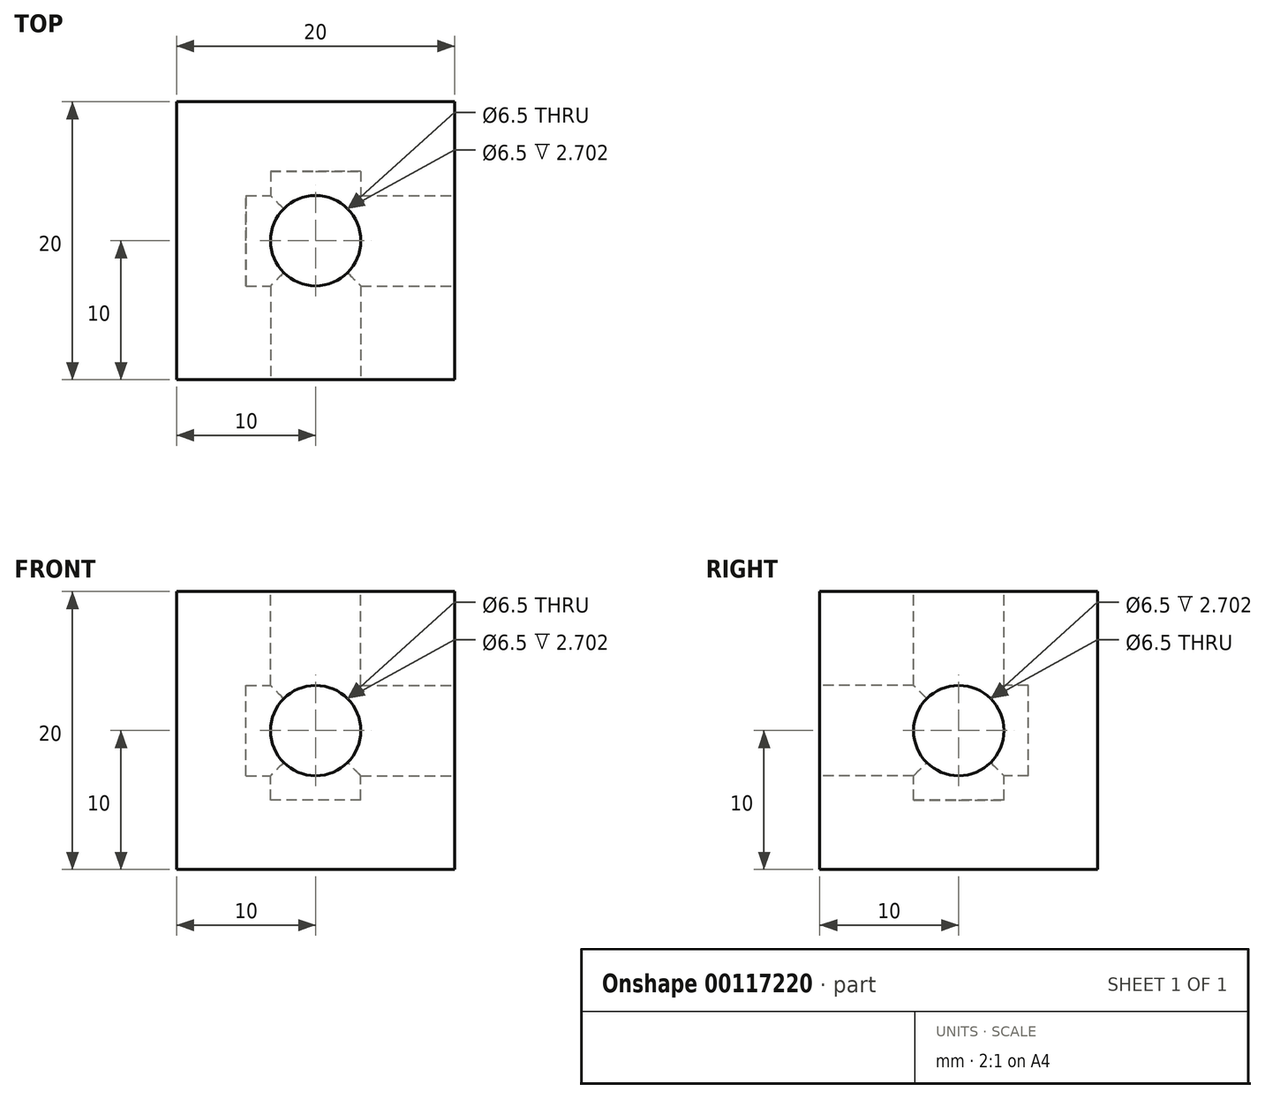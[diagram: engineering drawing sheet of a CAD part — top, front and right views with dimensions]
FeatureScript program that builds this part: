
annotation { "Feature Type Name" : "Feature", "Feature Type Description" : "" }
export const myFeature = defineFeature(function(context is Context, id is Id, definition is map)
    precondition{}
    {
        {
            var Q0;
            Q0=qCreatedBy(makeId("Top.planeOp"),FACE);
            var sketch = newSketch(context, id + "F0", { "sketchPlane" : qUnion([Q0])});
            skLineSegment(sketch, "E0.bottom", {"start": v(10, -10) * mm, "end": v(-10, -10) * mm});
            skLineSegment(sketch, "E0.top", {"start": v(10, 10) * mm, "end": v(-10, 10) * mm});
            skLineSegment(sketch, "E0.left", {"start": v(10, -10) * mm, "end": v(10, 10) * mm});
            skLineSegment(sketch, "E0.right", {"start": v(-10, -10) * mm, "end": v(-10, 10) * mm});
            skPoint(sketch, "E0.middle", {"position": v(0, 0) * mm});
            skSolve(sketch);
        }
        {
            var Q0;
            Q0=makeQuery(id+"F0.imprint","IMPRINT",FACE,{"disambiguationData":[TD([[makeQuery(id+"F0.imprint","IMPRINT",EDGE,{"derivedFrom":sQuery(id+"F0.wireOp",EDGE,"E0.bottom")}),-1.0]])]});
            extrude(context, id + "F1", {"entities" : qUnion([Q0]), "depth" : 20 * mm});
        }
        {
            var Q0;
            Q0=makeQuery(id+"F1.opExtrude","CAP_FACE",FACE,{"disambiguationData":[OSD([sQuery(id+"F0.wireOp",EDGE,"E0.bottom"),sQuery(id+"F0.wireOp",EDGE,"E0.top"),sQuery(id+"F0.wireOp",EDGE,"E0.left"),sQuery(id+"F0.wireOp",EDGE,"E0.right")])],"isStart":false});
            var sketch = newSketch(context, id + "F2", { "sketchPlane" : qUnion([Q0])});
            skCircle(sketch, "E1", {"center": v(0, 0) * mm, "radius": 3.25 * mm});
            skSolve(sketch);
        }
        {
            var Q0;
            Q0=makeQuery(id+"F2.imprint","IMPRINT",FACE,{"disambiguationData":[TD([[makeQuery(id+"F2.imprint","IMPRINT",EDGE,{"derivedFrom":sQuery(id+"F2.wireOp",EDGE,"E1")}),1.0]])]});
            extrude(context, id + "F3", {"entities" : qUnion([Q0]), "operationType" : NewBodyOperationType.REMOVE, "oppositeDirection" : true, "depth" : 15 * mm});
        }
        {
            var Q0;
            Q0=makeQuery(id+"F1.opExtrude","SWEPT_FACE",FACE,{"disambiguationData":[OSD([sQuery(id+"F0.wireOp",EDGE,"E0.bottom")])]});
            var sketch = newSketch(context, id + "F4", { "sketchPlane" : qUnion([Q0])});
            skLineSegment(sketch, "E2", {"start": v(10, 20) * mm, "end": v(-10, 0) * mm, "construction": true});
            skCircle(sketch, "E3", {"center": v(0, 10) * mm, "radius": 3.25 * mm});
            skSolve(sketch);
        }
        {
            var Q0;
            Q0=makeQuery(id+"F4.imprint","IMPRINT",FACE,{"disambiguationData":[TD([[makeQuery(id+"F4.imprint","IMPRINT",EDGE,{"derivedFrom":sQuery(id+"F4.wireOp",EDGE,"E3")}),1.0]])]});
            extrude(context, id + "F5", {"entities" : qUnion([Q0]), "operationType" : NewBodyOperationType.REMOVE, "oppositeDirection" : true, "depth" : 15 * mm});
        }
        {
            var Q0;
            Q0=makeQuery(id+"F1.opExtrude","SWEPT_FACE",FACE,{"disambiguationData":[OSD([sQuery(id+"F0.wireOp",EDGE,"E0.left")])]});
            var sketch = newSketch(context, id + "F6", { "sketchPlane" : qUnion([Q0])});
            skLineSegment(sketch, "E4", {"start": v(10, 20) * mm, "end": v(-10, 0) * mm, "construction": true});
            skCircle(sketch, "E5", {"center": v(0, 10) * mm, "radius": 3.25 * mm});
            skSolve(sketch);
        }
        {
            var Q0;
            Q0=makeQuery(id+"F6.imprint","IMPRINT",FACE,{"disambiguationData":[TD([[makeQuery(id+"F6.imprint","IMPRINT",EDGE,{"derivedFrom":sQuery(id+"F6.wireOp",EDGE,"E5")}),1.0]])]});
            extrude(context, id + "F7", {"entities" : qUnion([Q0]), "operationType" : NewBodyOperationType.REMOVE, "oppositeDirection" : true, "depth" : 15 * mm});
        }
    });
